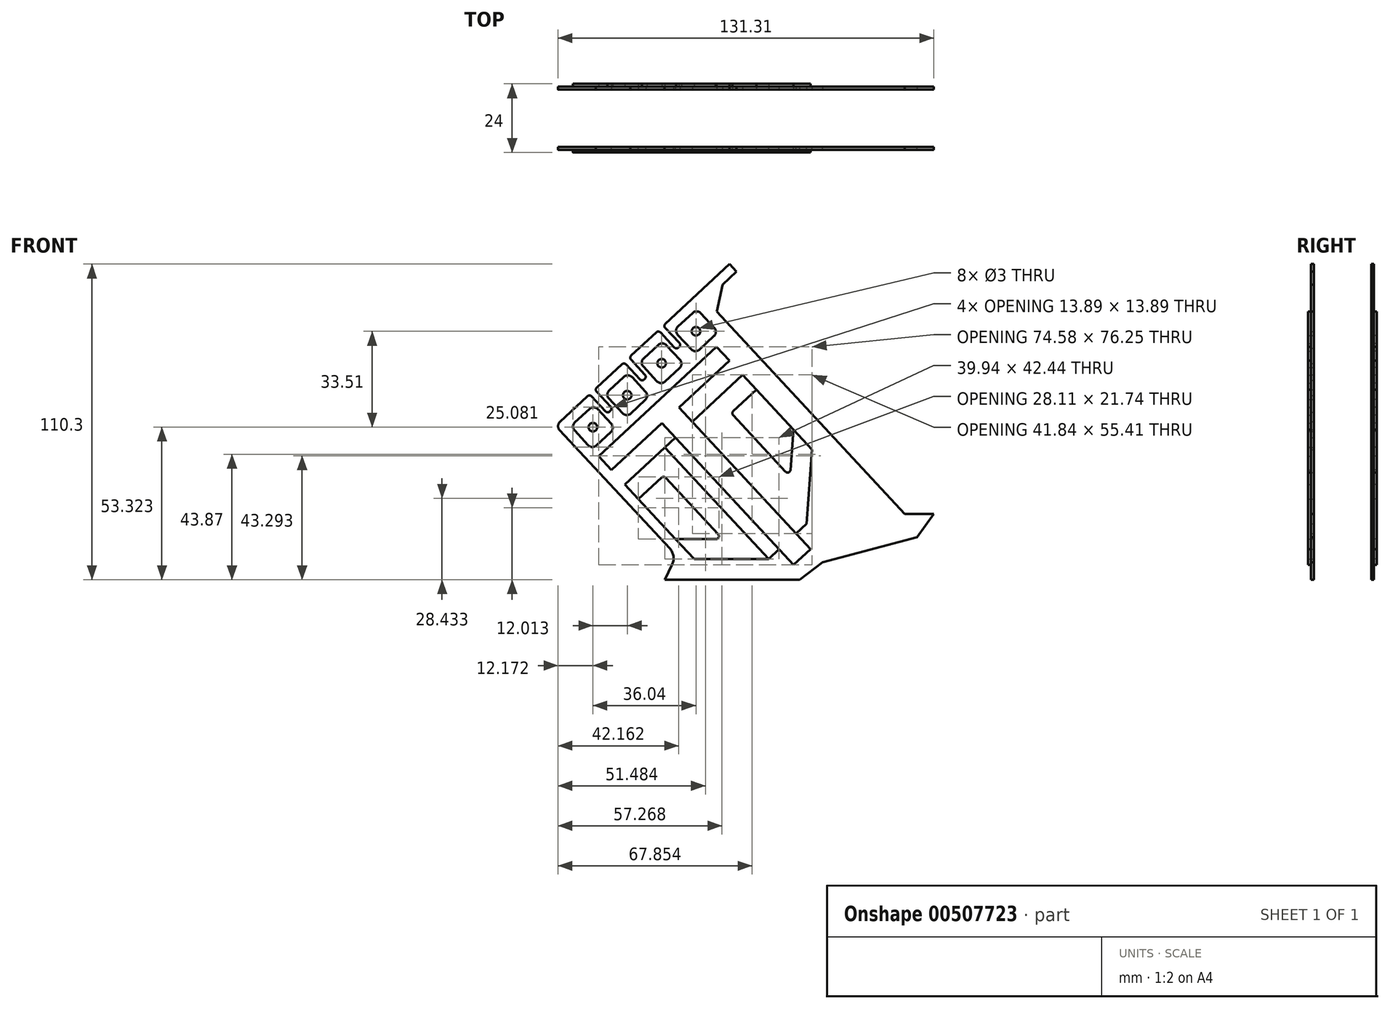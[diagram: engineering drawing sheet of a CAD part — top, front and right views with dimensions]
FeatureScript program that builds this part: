
annotation { "Feature Type Name" : "Feature", "Feature Type Description" : "" }
export const myFeature = defineFeature(function(context is Context, id is Id, definition is map)
    precondition{}
    {
        {
            var Q0;
            Q0=qCreatedBy(makeId("Front.planeOp"),FACE);
            var sketch = newSketch(context, id + "F0", { "sketchPlane" : qUnion([Q0])});
            skLineSegment(sketch, "E0", {"start": v(0, 0) * mm, "end": v(47.16, 0) * mm});
            skLineSegment(sketch, "E1", {"start": v(47.16, 0) * mm, "end": v(55.13, 6.04) * mm});
            skLineSegment(sketch, "E2", {"start": v(55.13, 6.04) * mm, "end": v(88.2, 14.9) * mm});
            skLineSegment(sketch, "E3", {"start": v(88.2, 14.9) * mm, "end": v(94.01, 23.05) * mm});
            skLineSegment(sketch, "E4", {"start": v(94.01, 23.05) * mm, "end": v(83.82, 23.05) * mm});
            skLineSegment(sketch, "E5", {"start": v(83.82, 23.05) * mm, "end": v(18.2, 93.67) * mm});
            skLineSegment(sketch, "E6", {"start": v(18.2, 93.67) * mm, "end": v(20.16, 103.12) * mm});
            skLineSegment(sketch, "E7", {"start": v(20.16, 103.12) * mm, "end": v(25.09, 107.7) * mm});
            skLineSegment(sketch, "E8", {"start": v(25.09, 107.7) * mm, "end": v(22.67, 110.3) * mm});
            skLineSegment(sketch, "E9", {"start": v(22.67, 110.3) * mm, "end": v(0.2, 89.41) * mm});
            skLineSegment(sketch, "E10", {"start": v(-36.77, 52.33) * mm, "end": v(1.74, 10.9) * mm});
            skLineSegment(sketch, "E11", {"start": v(0, 0) * mm, "end": v(2.58, 5.3) * mm});
            skPoint(sketch, "E12.visualSharp", {"position": v(4.07, 8.38) * mm});
            skArc(sketch, "E12.filletArc", {"start": v(2.58, 5.3) * mm, "mid": v(3.03, 8.23) * mm, "end": v(1.74, 10.9) * mm});
            skLineSegment(sketch, "E13.bottom", {"start": v(-31.44, 54.97) * mm, "end": v(-26.3, 59.73) * mm});
            skLineSegment(sketch, "E13.top", {"start": v(-23.95, 46.91) * mm, "end": v(-18.82, 51.68) * mm});
            skLineSegment(sketch, "E13.left", {"start": v(-31.54, 52.14) * mm, "end": v(-26.77, 47.02) * mm});
            skLineSegment(sketch, "E13.right", {"start": v(-23.48, 59.63) * mm, "end": v(-18.72, 54.5) * mm});
            skLineSegment(sketch, "E14", {"start": v(-28.87, 57.35) * mm, "end": v(-21.38, 49.3) * mm, "construction": true});
            skCircle(sketch, "E15", {"center": v(-25.13, 53.32) * mm, "radius": 1.5 * mm});
            skLineSegment(sketch, "E16.1.0.0", {"start": v(-19.42, 66.14) * mm, "end": v(-14.3, 70.9) * mm});
            skLineSegment(sketch, "E16.1.0.1", {"start": v(-16.86, 68.52) * mm, "end": v(-9.37, 60.46) * mm, "construction": true});
            skLineSegment(sketch, "E16.1.0.2", {"start": v(-11.47, 70.8) * mm, "end": v(-6.7, 65.67) * mm});
            skLineSegment(sketch, "E16.1.0.3", {"start": v(-19.53, 63.31) * mm, "end": v(-14.76, 58.19) * mm});
            skLineSegment(sketch, "E16.1.0.4", {"start": v(-11.93, 58.08) * mm, "end": v(-6.8, 62.85) * mm});
            skCircle(sketch, "E16.1.0.5", {"center": v(-13.11, 64.5) * mm, "radius": 1.5 * mm});
            skLineSegment(sketch, "E16.2.0.0", {"start": v(-7.4, 77.3) * mm, "end": v(-2.28, 82.07) * mm});
            skLineSegment(sketch, "E16.2.0.1", {"start": v(-4.85, 79.7) * mm, "end": v(2.64, 71.63) * mm, "construction": true});
            skLineSegment(sketch, "E16.2.0.2", {"start": v(0.54, 81.97) * mm, "end": v(5.3, 76.84) * mm});
            skLineSegment(sketch, "E16.2.0.3", {"start": v(-7.51, 74.48) * mm, "end": v(-2.75, 69.36) * mm});
            skLineSegment(sketch, "E16.2.0.4", {"start": v(0.08, 69.25) * mm, "end": v(5.2, 74.02) * mm});
            skCircle(sketch, "E16.2.0.5", {"center": v(-1.1, 75.66) * mm, "radius": 1.5 * mm});
            skLineSegment(sketch, "E16.3.0.0", {"start": v(4.6, 88.48) * mm, "end": v(9.73, 93.24) * mm});
            skLineSegment(sketch, "E16.3.0.1", {"start": v(7.17, 90.86) * mm, "end": v(14.66, 82.8) * mm, "construction": true});
            skLineSegment(sketch, "E16.3.0.2", {"start": v(12.56, 93.14) * mm, "end": v(17.32, 88.01) * mm});
            skLineSegment(sketch, "E16.3.0.3", {"start": v(4.5, 85.65) * mm, "end": v(9.27, 80.53) * mm});
            skLineSegment(sketch, "E16.3.0.4", {"start": v(12.1, 80.42) * mm, "end": v(17.22, 85.19) * mm});
            skCircle(sketch, "E16.3.0.5", {"center": v(10.91, 86.83) * mm, "radius": 1.5 * mm});
            skLineSegment(sketch, "E16.direction1", {"start": v(-25.41, 45.55) * mm, "end": v(-13.4, 56.72) * mm, "construction": true});
            skLineSegment(sketch, "E17", {"start": v(-23.1, 43.13) * mm, "end": v(18.1, 81.42) * mm});
            skLineSegment(sketch, "E18", {"start": v(-23.1, 43.13) * mm, "end": v(-18.64, 38.31) * mm});
            skLineSegment(sketch, "E19", {"start": v(-18.64, 38.31) * mm, "end": v(-1.02, 54.68) * mm});
            skLineSegment(sketch, "E20", {"start": v(-1.02, 54.68) * mm, "end": v(45, 5.17) * mm});
            skLineSegment(sketch, "E21", {"start": v(45, 5.17) * mm, "end": v(50.97, 10.72) * mm});
            skLineSegment(sketch, "E22", {"start": v(50.97, 10.72) * mm, "end": v(4.96, 60.24) * mm});
            skLineSegment(sketch, "E23", {"start": v(4.96, 60.24) * mm, "end": v(22.57, 76.6) * mm});
            skLineSegment(sketch, "E24", {"start": v(22.57, 76.6) * mm, "end": v(18.1, 81.42) * mm});
            skLineSegment(sketch, "E25", {"start": v(47.98, 7.95) * mm, "end": v(-2.5, 62.27) * mm, "construction": true});
            skLineSegment(sketch, "E26", {"start": v(-18.64, 38.31) * mm, "end": v(28.64, -12.56) * mm, "construction": true});
            skLineSegment(sketch, "E27", {"start": v(-13.96, 33.28) * mm, "end": v(-0.73, 45.58) * mm});
            skLineSegment(sketch, "E28", {"start": v(0.68, 45.52) * mm, "end": v(34.72, 8.9) * mm});
            skLineSegment(sketch, "E29", {"start": v(33.99, 7.21) * mm, "end": v(10.27, 7.21) * mm});
            skLineSegment(sketch, "E30.1", {"start": v(0.32, 35.63) * mm, "end": v(18.66, 15.9) * mm});
            skLineSegment(sketch, "E30.2", {"start": v(-9.2, 28.16) * mm, "end": v(-1.1, 35.68) * mm});
            skLineSegment(sketch, "E31", {"start": v(17.93, 14.21) * mm, "end": v(3.76, 14.21) * mm});
            skPoint(sketch, "E32.visualSharp", {"position": v(36.28, 7.21) * mm});
            skPoint(sketch, "E33.visualSharp", {"position": v(0, 46.26) * mm});
            skPoint(sketch, "E34.visualSharp", {"position": v(-0.36, 36.36) * mm});
            skArc(sketch, "E34.filletArc", {"start": v(0.32, 35.63) * mm, "mid": v(-0.38, 35.95) * mm, "end": v(-1.1, 35.68) * mm});
            skPoint(sketch, "E35.visualSharp", {"position": v(20.22, 14.21) * mm});
            skArc(sketch, "E35.filletArc", {"start": v(17.93, 14.21) * mm, "mid": v(18.84, 14.81) * mm, "end": v(18.66, 15.9) * mm});
            skArc(sketch, "E36.MirrorCS", {"start": v(43.93, 38.38) * mm, "mid": v(43.27, 37.5) * mm, "end": v(42.2, 37.77) * mm});
            skArc(sketch, "E37.MirrorCS", {"start": v(23.86, 57.5) * mm, "mid": v(23.6, 58.23) * mm, "end": v(23.91, 58.92) * mm});
            skLineSegment(sketch, "E38.MirrorCS", {"start": v(32.01, 66.45) * mm, "end": v(23.91, 58.92) * mm});
            skLineSegment(sketch, "E39.MirrorCS", {"start": v(23.86, 57.5) * mm, "end": v(42.2, 37.77) * mm});
            skLineSegment(sketch, "E40.MirrorCS", {"start": v(43.93, 38.38) * mm, "end": v(44.97, 52.5) * mm});
            skLineSegment(sketch, "E41.MirrorCS", {"start": v(49.74, 21.85) * mm, "end": v(51.47, 45.5) * mm});
            skLineSegment(sketch, "E42.MirrorCS", {"start": v(27.25, 71.58) * mm, "end": v(14.02, 59.28) * mm});
            skLineSegment(sketch, "E43.MirrorCS", {"start": v(13.97, 57.87) * mm, "end": v(48, 21.24) * mm});
            skLineSegment(sketch, "E44", {"start": v(-13.96, 33.28) * mm, "end": v(-9.2, 28.16) * mm});
            skLineSegment(sketch, "E45", {"start": v(3.76, 14.21) * mm, "end": v(10.27, 7.21) * mm});
            skLineSegment(sketch, "E46", {"start": v(27.25, 71.58) * mm, "end": v(32.01, 66.45) * mm});
            skLineSegment(sketch, "E47", {"start": v(44.97, 52.5) * mm, "end": v(51.47, 45.5) * mm});
            skPoint(sketch, "E48.visualSharp", {"position": v(-32.9, 53.6) * mm});
            skArc(sketch, "E48.filletArc", {"start": v(-31.44, 54.97) * mm, "mid": v(-32.07, 53.58) * mm, "end": v(-31.54, 52.14) * mm});
            skPoint(sketch, "E49.visualSharp", {"position": v(-25.41, 45.55) * mm});
            skArc(sketch, "E49.filletArc", {"start": v(-26.77, 47.02) * mm, "mid": v(-25.38, 46.38) * mm, "end": v(-23.95, 46.91) * mm});
            skPoint(sketch, "E50.visualSharp", {"position": v(-17.36, 53.04) * mm});
            skArc(sketch, "E50.filletArc", {"start": v(-18.82, 51.68) * mm, "mid": v(-18.18, 53.07) * mm, "end": v(-18.72, 54.5) * mm});
            skPoint(sketch, "E51.visualSharp", {"position": v(-24.84, 61.1) * mm});
            skArc(sketch, "E51.filletArc", {"start": v(-23.48, 59.63) * mm, "mid": v(-24.87, 60.27) * mm, "end": v(-26.3, 59.73) * mm});
            skPoint(sketch, "E52.visualSharp", {"position": v(-20.89, 64.78) * mm});
            skArc(sketch, "E52.filletArc", {"start": v(-19.42, 66.14) * mm, "mid": v(-20.06, 64.75) * mm, "end": v(-19.53, 63.31) * mm});
            skPoint(sketch, "E53.visualSharp", {"position": v(-13.4, 56.72) * mm});
            skArc(sketch, "E53.filletArc", {"start": v(-14.76, 58.19) * mm, "mid": v(-13.37, 57.55) * mm, "end": v(-11.93, 58.08) * mm});
            skPoint(sketch, "E54.visualSharp", {"position": v(-5.34, 64.2) * mm});
            skArc(sketch, "E54.filletArc", {"start": v(-6.8, 62.85) * mm, "mid": v(-6.17, 64.24) * mm, "end": v(-6.7, 65.67) * mm});
            skPoint(sketch, "E55.visualSharp", {"position": v(-12.83, 72.27) * mm});
            skArc(sketch, "E55.filletArc", {"start": v(-11.47, 70.8) * mm, "mid": v(-12.86, 71.44) * mm, "end": v(-14.3, 70.9) * mm});
            skPoint(sketch, "E56.visualSharp", {"position": v(-8.87, 75.95) * mm});
            skArc(sketch, "E56.filletArc", {"start": v(-7.4, 77.3) * mm, "mid": v(-8.05, 75.92) * mm, "end": v(-7.51, 74.48) * mm});
            skPoint(sketch, "E57.visualSharp", {"position": v(-1.39, 67.9) * mm});
            skArc(sketch, "E57.filletArc", {"start": v(-2.75, 69.36) * mm, "mid": v(-1.36, 68.72) * mm, "end": v(0.08, 69.25) * mm});
            skPoint(sketch, "E58.visualSharp", {"position": v(6.67, 75.38) * mm});
            skArc(sketch, "E58.filletArc", {"start": v(5.2, 74.02) * mm, "mid": v(5.84, 75.4) * mm, "end": v(5.3, 76.84) * mm});
            skPoint(sketch, "E59.visualSharp", {"position": v(-0.82, 83.44) * mm});
            skArc(sketch, "E59.filletArc", {"start": v(0.54, 81.97) * mm, "mid": v(-0.85, 82.6) * mm, "end": v(-2.28, 82.07) * mm});
            skPoint(sketch, "E60.visualSharp", {"position": v(3.14, 87.12) * mm});
            skArc(sketch, "E60.filletArc", {"start": v(4.6, 88.48) * mm, "mid": v(3.97, 87.09) * mm, "end": v(4.5, 85.65) * mm});
            skPoint(sketch, "E61.visualSharp", {"position": v(10.63, 79.06) * mm});
            skArc(sketch, "E61.filletArc", {"start": v(9.27, 80.53) * mm, "mid": v(10.66, 79.89) * mm, "end": v(12.1, 80.42) * mm});
            skPoint(sketch, "E62.visualSharp", {"position": v(18.68, 86.55) * mm});
            skArc(sketch, "E62.filletArc", {"start": v(17.22, 85.19) * mm, "mid": v(17.86, 86.58) * mm, "end": v(17.32, 88.01) * mm});
            skPoint(sketch, "E63.visualSharp", {"position": v(11.2, 94.6) * mm});
            skArc(sketch, "E63.filletArc", {"start": v(12.56, 93.14) * mm, "mid": v(11.17, 93.78) * mm, "end": v(9.73, 93.24) * mm});
            skPoint(sketch, "E64.visualSharp", {"position": v(-38.13, 53.8) * mm});
            skArc(sketch, "E64.filletArc", {"start": v(-36.67, 55.16) * mm, "mid": v(-37.3, 53.77) * mm, "end": v(-36.77, 52.33) * mm});
            skPoint(sketch, "E65", {"position": v(-22.38, 60.65) * mm});
            skPoint(sketch, "E66", {"position": v(-20.62, 62.3) * mm});
            skLineSegment(sketch, "E67.trimOffspring", {"start": v(-27, 64.14) * mm, "end": v(-36.67, 55.16) * mm});
            skPoint(sketch, "E68.visualSharp", {"position": v(-24.5, 66.46) * mm});
            skArc(sketch, "E68.filletArc", {"start": v(-23.77, 67.14) * mm, "mid": v(-24.09, 66.45) * mm, "end": v(-23.82, 65.73) * mm});
            skPoint(sketch, "E69.visualSharp", {"position": v(-26.27, 64.82) * mm});
            skArc(sketch, "E69.filletArc", {"start": v(-25.59, 64.1) * mm, "mid": v(-26.28, 64.41) * mm, "end": v(-27, 64.14) * mm});
            skPoint(sketch, "E70", {"position": v(-21.1, 57.07) * mm});
            skLineSegment(sketch, "E71", {"start": v(-21.1, 57.07) * mm, "end": v(-17.14, 60.75) * mm, "construction": true});
            skLineSegment(sketch, "E72", {"start": v(-25.59, 64.1) * mm, "end": v(-20.68, 58.82) * mm});
            skLineSegment(sketch, "E73", {"start": v(-23.82, 65.73) * mm, "end": v(-18.92, 60.46) * mm});
            skLineSegment(sketch, "E74", {"start": v(-18.97, 59.04) * mm, "end": v(-19.27, 58.77) * mm});
            skPoint(sketch, "E75.visualSharp", {"position": v(-20, 58.1) * mm});
            skArc(sketch, "E75.filletArc", {"start": v(-20.68, 58.82) * mm, "mid": v(-19.98, 58.5) * mm, "end": v(-19.27, 58.77) * mm});
            skPoint(sketch, "E76.visualSharp", {"position": v(-18.24, 59.72) * mm});
            skArc(sketch, "E76.filletArc", {"start": v(-18.97, 59.04) * mm, "mid": v(-18.65, 59.74) * mm, "end": v(-18.92, 60.46) * mm});
            skLineSegment(sketch, "E77", {"start": v(-9.09, 68.24) * mm, "end": v(-5.13, 71.92) * mm, "construction": true});
            skLineSegment(sketch, "E78", {"start": v(2.93, 79.4) * mm, "end": v(6.89, 83.09) * mm, "construction": true});
            skPoint(sketch, "E79", {"position": v(-7.99, 69.26) * mm});
            skPoint(sketch, "E80", {"position": v(-6.23, 70.9) * mm});
            skPoint(sketch, "E81", {"position": v(4.03, 80.43) * mm});
            skPoint(sketch, "E82", {"position": v(5.79, 82.06) * mm});
            skLineSegment(sketch, "E83", {"start": v(-8.67, 70) * mm, "end": v(-13.57, 75.26) * mm});
            skLineSegment(sketch, "E84", {"start": v(-6.9, 71.63) * mm, "end": v(-11.8, 76.9) * mm});
            skLineSegment(sketch, "E85", {"start": v(-7.25, 69.94) * mm, "end": v(-6.96, 70.21) * mm});
            skLineSegment(sketch, "E86", {"start": v(3.35, 81.16) * mm, "end": v(-1.55, 86.43) * mm});
            skLineSegment(sketch, "E87", {"start": v(5.09, 82.8) * mm, "end": v(0.15, 87.99) * mm});
            skLineSegment(sketch, "E88", {"start": v(4.76, 81.1) * mm, "end": v(5.05, 81.38) * mm});
            skLineSegment(sketch, "E89.trimOffspring", {"start": v(-14.98, 75.31) * mm, "end": v(-23.77, 67.14) * mm});
            skLineSegment(sketch, "E90.trimOffspring", {"start": v(-2.96, 86.48) * mm, "end": v(-11.75, 78.31) * mm});
            skPoint(sketch, "E91.visualSharp", {"position": v(-14.25, 76) * mm});
            skArc(sketch, "E91.filletArc", {"start": v(-13.57, 75.26) * mm, "mid": v(-14.26, 75.58) * mm, "end": v(-14.98, 75.31) * mm});
            skPoint(sketch, "E92.visualSharp", {"position": v(-12.49, 77.63) * mm});
            skArc(sketch, "E92.filletArc", {"start": v(-11.75, 78.31) * mm, "mid": v(-12.07, 77.61) * mm, "end": v(-11.8, 76.9) * mm});
            skArc(sketch, "E93.filletArc", {"start": v(-8.67, 70) * mm, "mid": v(-7.97, 69.67) * mm, "end": v(-7.25, 69.94) * mm});
            skArc(sketch, "E94.filletArc", {"start": v(-6.96, 70.21) * mm, "mid": v(-6.64, 70.9) * mm, "end": v(-6.9, 71.63) * mm});
            skPoint(sketch, "E95.visualSharp", {"position": v(-2.23, 87.16) * mm});
            skArc(sketch, "E95.filletArc", {"start": v(-1.55, 86.43) * mm, "mid": v(-2.24, 86.75) * mm, "end": v(-2.96, 86.48) * mm});
            skPoint(sketch, "E96.visualSharp", {"position": v(-0.55, 88.72) * mm});
            skArc(sketch, "E96.filletArc", {"start": v(0.2, 89.41) * mm, "mid": v(-0.13, 88.7) * mm, "end": v(0.15, 87.99) * mm});
            skArc(sketch, "E97.filletArc", {"start": v(3.35, 81.16) * mm, "mid": v(4.04, 80.84) * mm, "end": v(4.76, 81.1) * mm});
            skArc(sketch, "E98.filletArc", {"start": v(5.05, 81.38) * mm, "mid": v(5.36, 82.08) * mm, "end": v(5.09, 82.8) * mm});
            skLineSegment(sketch, "E99", {"start": v(-9.2, 28.16) * mm, "end": v(3.76, 14.21) * mm});
            skLineSegment(sketch, "E100.MirrorCS", {"start": v(6.77, -30.35) * mm, "end": v(-43.71, 23.98) * mm, "construction": true});
            skLineSegment(sketch, "E101", {"start": v(32.01, 66.45) * mm, "end": v(44.97, 52.5) * mm});
            skLineSegment(sketch, "E102", {"start": v(-0.73, 45.58) * mm, "end": v(0, 46.26) * mm});
            skLineSegment(sketch, "E103", {"start": v(0, 46.26) * mm, "end": v(0.68, 45.52) * mm});
            skLineSegment(sketch, "E104", {"start": v(0, 46.26) * mm, "end": v(3.65, 49.65) * mm});
            skLineSegment(sketch, "E105", {"start": v(33.99, 7.21) * mm, "end": v(36.28, 7.21) * mm});
            skLineSegment(sketch, "E106", {"start": v(34.72, 8.9) * mm, "end": v(36.28, 7.21) * mm});
            skLineSegment(sketch, "E107", {"start": v(36.28, 7.21) * mm, "end": v(39.94, 10.6) * mm});
            skLineSegment(sketch, "E108.MirrorCS", {"start": v(48, 21.24) * mm, "end": v(49.57, 19.56) * mm});
            skLineSegment(sketch, "E109.MirrorCS", {"start": v(49.74, 21.85) * mm, "end": v(49.57, 19.56) * mm});
            skLineSegment(sketch, "E110.MirrorCS", {"start": v(49.57, 19.56) * mm, "end": v(45.91, 16.16) * mm});
            skLineSegment(sketch, "E111.MirrorCS", {"start": v(14.02, 59.28) * mm, "end": v(13.29, 58.6) * mm});
            skLineSegment(sketch, "E112.MirrorCS", {"start": v(13.29, 58.6) * mm, "end": v(13.97, 57.87) * mm});
            skLineSegment(sketch, "E113.MirrorCS", {"start": v(13.29, 58.6) * mm, "end": v(9.63, 55.2) * mm});
            skSolve(sketch);
        }
        {
            var Q0;
            Q0=makeQuery(id+"F0.imprint","IMPRINT",FACE,{"disambiguationData":[TD([[makeQuery(id+"F0.imprint","IMPRINT",EDGE,{"derivedFrom":sQuery(id+"F0.wireOp",EDGE,"E0")}),1.0]])]});
            extrude(context, id + "F1", {"entities" : qUnion([Q0]), "depth" : 1 * mm, "offsetDistance" : 25 * mm});
        }
        {
            var Q0;
            Q0=makeQuery(id+"F0.imprint","IMPRINT",FACE,{"disambiguationData":[TD([[makeQuery(id+"F0.imprint","IMPRINT",EDGE,{"derivedFrom":sQuery(id+"F0.wireOp",EDGE,"E16.3.0.0")}),-1.0]])]});
            var Q1;
            Q1=makeQuery(id+"F0.imprint","IMPRINT",FACE,{"disambiguationData":[TD([[makeQuery(id+"F0.imprint","IMPRINT",EDGE,{"derivedFrom":sQuery(id+"F0.wireOp",EDGE,"E16.2.0.0")}),-1.0]])]});
            var Q2;
            Q2=makeQuery(id+"F0.imprint","IMPRINT",FACE,{"disambiguationData":[TD([[makeQuery(id+"F0.imprint","IMPRINT",EDGE,{"derivedFrom":sQuery(id+"F0.wireOp",EDGE,"E16.1.0.0")}),-1.0]])]});
            var Q3;
            Q3=makeQuery(id+"F0.imprint","IMPRINT",FACE,{"disambiguationData":[TD([[makeQuery(id+"F0.imprint","IMPRINT",EDGE,{"derivedFrom":sQuery(id+"F0.wireOp",EDGE,"E13.bottom")}),-1.0]])]});
            var Q4;
            Q4=makeQuery(id+"F0.imprint","IMPRINT",FACE,{"disambiguationData":[TD([[makeQuery(id+"F0.imprint","IMPRINT",EDGE,{"derivedFrom":sQuery(id+"F0.wireOp",EDGE,"E17")}),-1.0]])]});
            var Q5;
            Q5=makeQuery(id+"F0.imprint","IMPRINT",FACE,{"disambiguationData":[TD([[makeQuery(id+"F0.imprint","IMPRINT",EDGE,{"derivedFrom":sQuery(id+"F0.wireOp",EDGE,"E36.MirrorCS")}),1.0]])]});
            var Q6;
            Q6=makeQuery(id+"F0.imprint","IMPRINT",FACE,{"disambiguationData":[TD([[makeQuery(id+"F0.imprint","IMPRINT",EDGE,{"derivedFrom":sQuery(id+"F0.wireOp",EDGE,"E27")}),-1.0]])]});
            extrude(context, id + "F2", {"entities" : qUnion([Q0, Q1, Q2, Q3, Q4, Q5, Q6]), "operationType" : NewBodyOperationType.ADD, "depth" : 2 * mm, "offsetDistance" : 25 * mm});
        }
        {
            var Q0;
            Q0=qCreatedBy(makeId("Front.planeOp"),FACE);
            cPlane(context, id + "F3", {"entities" : qUnion([Q0]), "cplaneType" : CPlaneType.OFFSET, "offset" : 10 * mm, "oppositeDirection" : true, "width" : 150 * mm, "height" : 150 * mm});
        }
        {
            var Q0;
            Q0=makeQuery(id+"F1.opExtrude","SWEPT_BODY",BODY,{"disambiguationData":[OSD([sQuery(id+"F0.wireOp",EDGE,"E0"),sQuery(id+"F0.wireOp",EDGE,"E1"),sQuery(id+"F0.wireOp",EDGE,"E2"),sQuery(id+"F0.wireOp",EDGE,"E3"),sQuery(id+"F0.wireOp",EDGE,"E4"),sQuery(id+"F0.wireOp",EDGE,"E5"),sQuery(id+"F0.wireOp",EDGE,"E6"),sQuery(id+"F0.wireOp",EDGE,"E7"),sQuery(id+"F0.wireOp",EDGE,"E8"),sQuery(id+"F0.wireOp",EDGE,"E9"),sQuery(id+"F0.wireOp",EDGE,"E10"),sQuery(id+"F0.wireOp",EDGE,"E11"),sQuery(id+"F0.wireOp",EDGE,"E12.filletArc"),sQuery(id+"F0.wireOp",EDGE,"E13.bottom"),sQuery(id+"F0.wireOp",EDGE,"E13.top"),sQuery(id+"F0.wireOp",EDGE,"E13.left"),sQuery(id+"F0.wireOp",EDGE,"E13.right"),sQuery(id+"F0.wireOp",EDGE,"E16.1.0.0"),sQuery(id+"F0.wireOp",EDGE,"E16.1.0.2"),sQuery(id+"F0.wireOp",EDGE,"E16.1.0.3"),sQuery(id+"F0.wireOp",EDGE,"E16.1.0.4"),sQuery(id+"F0.wireOp",EDGE,"E16.2.0.0"),sQuery(id+"F0.wireOp",EDGE,"E16.2.0.2"),sQuery(id+"F0.wireOp",EDGE,"E16.2.0.3"),sQuery(id+"F0.wireOp",EDGE,"E16.2.0.4"),sQuery(id+"F0.wireOp",EDGE,"E16.3.0.0"),sQuery(id+"F0.wireOp",EDGE,"E16.3.0.2"),sQuery(id+"F0.wireOp",EDGE,"E16.3.0.3"),sQuery(id+"F0.wireOp",EDGE,"E16.3.0.4"),sQuery(id+"F0.wireOp",EDGE,"E17"),sQuery(id+"F0.wireOp",EDGE,"E18"),sQuery(id+"F0.wireOp",EDGE,"E19"),sQuery(id+"F0.wireOp",EDGE,"E20"),sQuery(id+"F0.wireOp",EDGE,"E21"),sQuery(id+"F0.wireOp",EDGE,"E22"),sQuery(id+"F0.wireOp",EDGE,"E23"),sQuery(id+"F0.wireOp",EDGE,"E24"),sQuery(id+"F0.wireOp",EDGE,"E27"),sQuery(id+"F0.wireOp",EDGE,"E28"),sQuery(id+"F0.wireOp",EDGE,"E29"),sQuery(id+"F0.wireOp",EDGE,"E30.1"),sQuery(id+"F0.wireOp",EDGE,"E30.2"),sQuery(id+"F0.wireOp",EDGE,"E31"),sQuery(id+"F0.wireOp",EDGE,"E32.filletArc"),sQuery(id+"F0.wireOp",EDGE,"E33.filletArc"),sQuery(id+"F0.wireOp",EDGE,"E34.filletArc"),sQuery(id+"F0.wireOp",EDGE,"E35.filletArc"),sQuery(id+"F0.wireOp",EDGE,"fae8f853-1109-4c4c-ad1f-c05ec79afbff0.MirrorCS"),sQuery(id+"F0.wireOp",EDGE,"E36.MirrorCS"),sQuery(id+"F0.wireOp",EDGE,"fae8f853-1109-4c4c-ad1f-c05ec79afbff2.MirrorCS"),sQuery(id+"F0.wireOp",EDGE,"E37.MirrorCS"),sQuery(id+"F0.wireOp",EDGE,"E38.MirrorCS"),sQuery(id+"F0.wireOp",EDGE,"E39.MirrorCS"),sQuery(id+"F0.wireOp",EDGE,"E40.MirrorCS"),sQuery(id+"F0.wireOp",EDGE,"E41.MirrorCS"),sQuery(id+"F0.wireOp",EDGE,"E42.MirrorCS"),sQuery(id+"F0.wireOp",EDGE,"E43.MirrorCS"),sQuery(id+"F0.wireOp",EDGE,"E44"),sQuery(id+"F0.wireOp",EDGE,"E45"),sQuery(id+"F0.wireOp",EDGE,"E46"),sQuery(id+"F0.wireOp",EDGE,"E47")])]});
            var Q1;
            Q1=qCreatedBy(id+"F3.planeOp",FACE);
            mirror(context, id + "F4", {"entities" : qUnion([Q0]), "mirrorPlane" : qUnion([Q1])});
        }
    });
